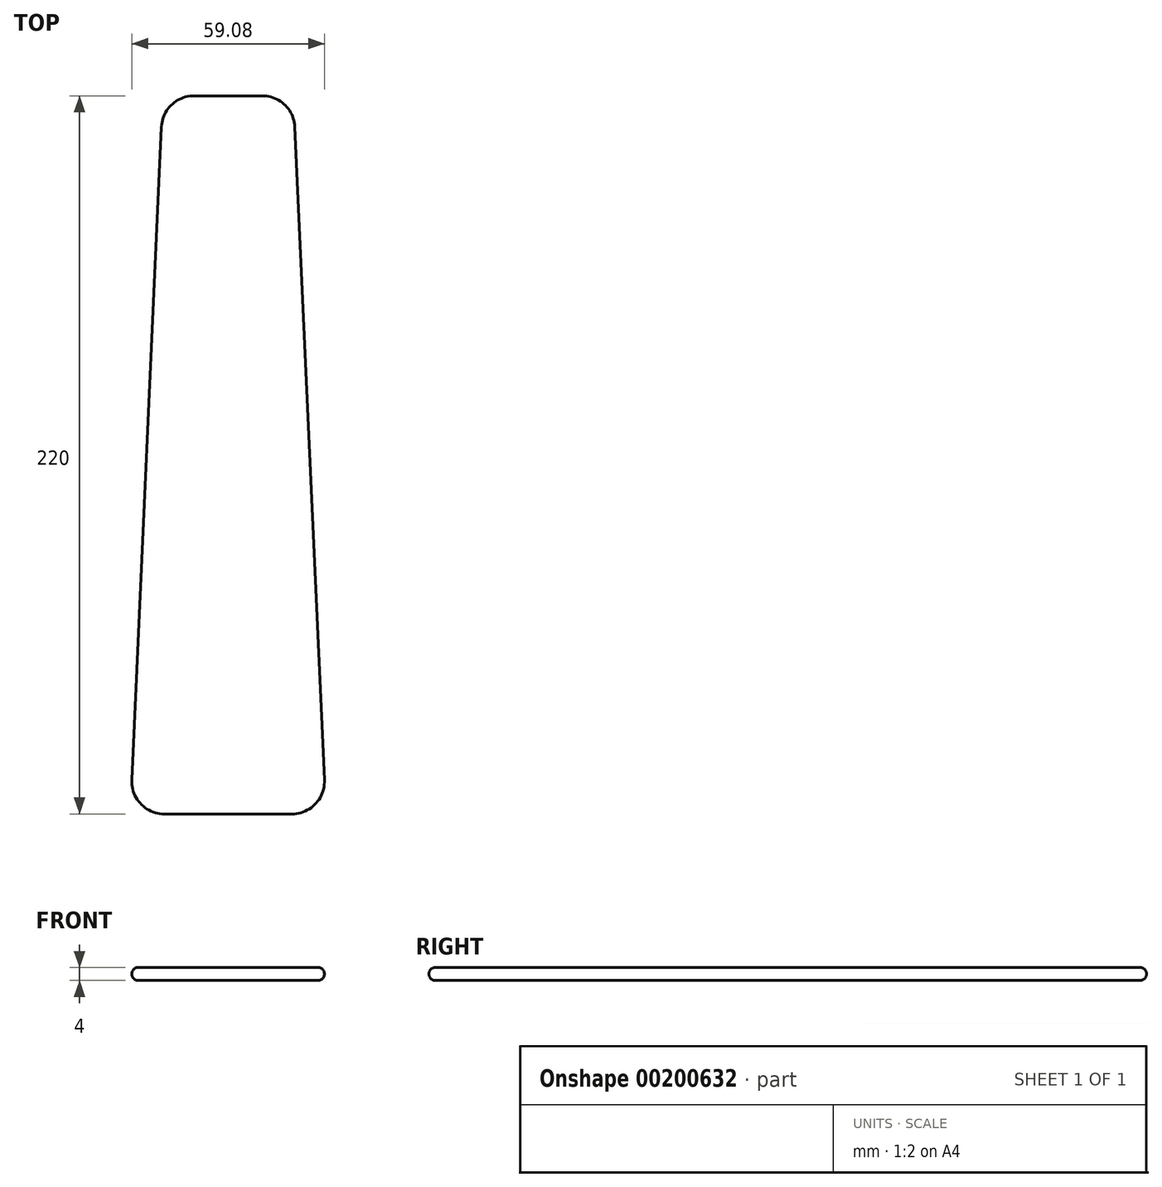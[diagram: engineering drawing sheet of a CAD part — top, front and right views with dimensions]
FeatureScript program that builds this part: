
annotation { "Feature Type Name" : "Feature", "Feature Type Description" : "" }
export const myFeature = defineFeature(function(context is Context, id is Id, definition is map)
    precondition{}
    {
        {
            var Q0;
            Q0=qCreatedBy(makeId("Top.planeOp"),FACE);
            var sketch = newSketch(context, id + "F0", { "sketchPlane" : qUnion([Q0])});
            skPoint(sketch, "E0.middle", {"position": v(0, 0) * mm});
            skLineSegment(sketch, "E1", {"start": v(0, 110) * mm, "end": v(-10.44, 110) * mm});
            skLineSegment(sketch, "E2", {"start": v(-20.43, 100.45) * mm, "end": v(-29.52, -99.55) * mm});
            skLineSegment(sketch, "E3", {"start": v(-19.54, -110) * mm, "end": v(0, -110) * mm});
            skLineSegment(sketch, "E4", {"start": v(0, -118.33) * mm, "end": v(0, 133.16) * mm, "construction": true});
            skLineSegment(sketch, "E5.MirrorCS", {"start": v(0, 110) * mm, "end": v(10.44, 110) * mm});
            skLineSegment(sketch, "E6.MirrorCS", {"start": v(20.43, 100.45) * mm, "end": v(29.52, -99.55) * mm});
            skLineSegment(sketch, "E7.MirrorCS", {"start": v(19.54, -110) * mm, "end": v(0, -110) * mm});
            skPoint(sketch, "E8", {"position": v(-25, 0) * mm});
            skPoint(sketch, "E9", {"position": v(25, 0) * mm});
            skPoint(sketch, "E10.visualSharp", {"position": v(-20, 110) * mm});
            skArc(sketch, "E10.filletArc", {"start": v(-10.44, 110) * mm, "mid": v(-17.35, 107.23) * mm, "end": v(-20.43, 100.45) * mm});
            skPoint(sketch, "E11.visualSharp", {"position": v(20, 110) * mm});
            skArc(sketch, "E11.filletArc", {"start": v(20.43, 100.45) * mm, "mid": v(17.35, 107.23) * mm, "end": v(10.44, 110) * mm});
            skPoint(sketch, "E12.visualSharp", {"position": v(-30, -110) * mm});
            skArc(sketch, "E12.filletArc", {"start": v(-29.52, -99.55) * mm, "mid": v(-26.76, -106.9) * mm, "end": v(-19.54, -110) * mm});
            skPoint(sketch, "E13.visualSharp", {"position": v(30, -110) * mm});
            skArc(sketch, "E13.filletArc", {"start": v(19.54, -110) * mm, "mid": v(26.76, -106.9) * mm, "end": v(29.52, -99.55) * mm});
            skSolve(sketch);
        }
        {
            var Q0;
            Q0 = qSketchRegion(id + "F0", true);
            extrude(context, id + "F1", {"entities" : qUnion([Q0]), "depth" : 4 * mm});
        }
        {
            var Q0;
            Q0=makeQuery(id+"F1.opExtrude","CAP_EDGE",EDGE,{"disambiguationData":[OSD([sQuery(id+"F0.wireOp",EDGE,"E2")])],"isStart":false});
            var Q1;
            Q1=makeQuery(id+"F1.opExtrude","CAP_EDGE",EDGE,{"disambiguationData":[OSD([sQuery(id+"F0.wireOp",EDGE,"E2")])],"isStart":true});
            fillet(context, id + "F2", {"entities" : qUnion([Q0, Q1]), "radius" : 2 * mm, "tangentPropagation" : true, "allowEdgeOverflow" : false});
        }
    });
